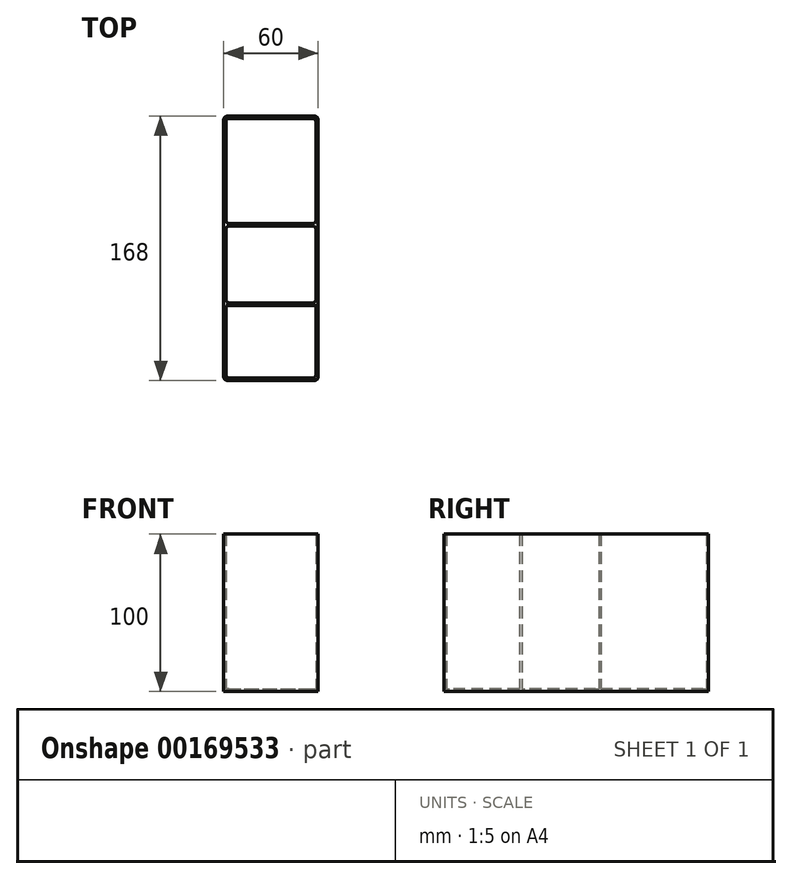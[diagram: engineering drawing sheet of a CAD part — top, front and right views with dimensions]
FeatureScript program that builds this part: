
annotation { "Feature Type Name" : "Feature", "Feature Type Description" : "" }
export const myFeature = defineFeature(function(context is Context, id is Id, definition is map)
    precondition{}
    {
        {
            var Q0;
            Q0=qCreatedBy(makeId("Top.planeOp"),FACE);
            var sketch = newSketch(context, id + "F0", { "sketchPlane" : qUnion([Q0])});
            skLineSegment(sketch, "E0.bottom", {"start": v(-30, 84) * mm, "end": v(30, 84) * mm});
            skLineSegment(sketch, "E0.top", {"start": v(-30, -84) * mm, "end": v(30, -84) * mm});
            skLineSegment(sketch, "E0.left", {"start": v(-30, 84) * mm, "end": v(-30, -84) * mm});
            skLineSegment(sketch, "E0.right", {"start": v(30, 84) * mm, "end": v(30, -84) * mm});
            skPoint(sketch, "E0.middle", {"position": v(0, 0) * mm});
            skSolve(sketch);
        }
        {
            var Q0;
            Q0 = qSketchRegion(id + "F0", true);
            extrude(context, id + "F1", {"entities" : qUnion([Q0]), "depth" : 100 * mm});
        }
        {
            var Q0;
            Q0=makeQuery(id+"F1.opExtrude","CAP_FACE",FACE,{"disambiguationData":[OSD([sQuery(id+"F0.wireOp",EDGE,"E0.bottom"),sQuery(id+"F0.wireOp",EDGE,"E0.top"),sQuery(id+"F0.wireOp",EDGE,"E0.left"),sQuery(id+"F0.wireOp",EDGE,"E0.right")])],"isStart":false});
            shell(context, id + "F2", {"entities" : qUnion([Q0]), "thickness" : 1.5 * mm});
        }
        {
            var Q0;
            Q0=makeQuery(id+"F2.opShell","OFFSET_FACE",FACE,{"disambiguationData":[OSD([sQuery(id+"F0.wireOp",EDGE,"E0.bottom"),sQuery(id+"F0.wireOp",EDGE,"E0.top"),sQuery(id+"F0.wireOp",EDGE,"E0.left"),sQuery(id+"F0.wireOp",EDGE,"E0.right")])]});
            var sketch = newSketch(context, id + "F3", { "sketchPlane" : qUnion([Q0])});
            skLineSegment(sketch, "E1", {"start": v(-28.5, 14.2) * mm, "end": v(28.5, 14.2) * mm});
            skLineSegment(sketch, "E2", {"start": v(-28.5, 15.7) * mm, "end": v(28.5, 15.7) * mm});
            skLineSegment(sketch, "E3", {"start": v(-28.5, -36.2) * mm, "end": v(28.5, -36.2) * mm});
            skLineSegment(sketch, "E4", {"start": v(-28.5, -34.7) * mm, "end": v(28.5, -34.7) * mm});
            skSolve(sketch);
        }
        {
            var Q0;
            {var subQ0=sQuery(id+"F3.wireOp",EDGE,"E1");Q0=makeQuery(id+"F3.imprint","IMPRINT",FACE,{"disambiguationData":[TD([[makeQuery(id+"F3.imprint","IMPRINT",EDGE,{"derivedFrom":subQ0}),1.0]])]});}
            var Q1;
            {var subQ0=sQuery(id+"F3.wireOp",EDGE,"E3");Q1=makeQuery(id+"F3.imprint","IMPRINT",FACE,{"disambiguationData":[TD([[makeQuery(id+"F3.imprint","IMPRINT",EDGE,{"derivedFrom":subQ0}),1.0]])]});}
            var Q2;
            Q2=makeQuery(id+"F1.opExtrude","CAP_FACE",FACE,{"disambiguationData":[OSD([sQuery(id+"F0.wireOp",EDGE,"E0.bottom"),sQuery(id+"F0.wireOp",EDGE,"E0.top"),sQuery(id+"F0.wireOp",EDGE,"E0.left"),sQuery(id+"F0.wireOp",EDGE,"E0.right")])],"isStart":false});
            extrude(context, id + "F4", {"entities" : qUnion([Q0, Q1]), "operationType" : NewBodyOperationType.ADD, "endBound" : BoundingType.UP_TO_SURFACE, "endBoundEntityFace" : qUnion([Q2]), "depth" : 25 * mm});
        }
        {
            var Q0;
            Q0=makeQuery(id+"F2.opShell","OFFSET_EDGE",EDGE,{"disambiguationData":[OSD([sQuery(id+"F0.wireOp",EDGE,"E0.top"),sQuery(id+"F0.wireOp",EDGE,"E0.left")])]});
            var Q1;
            Q1=makeQuery(id+"F4.opExtrude","SWEPT_EDGE",EDGE,{"disambiguationData":[OSD([sQuery(id+"F0.wireOp",EDGE,"E0.left"),sQuery(id+"F3.wireOp",EDGE,"E1")])]});
            var Q2;
            Q2=makeQuery(id+"F2.opShell","OFFSET_EDGE",EDGE,{"disambiguationData":[OSD([sQuery(id+"F0.wireOp",EDGE,"E0.bottom"),sQuery(id+"F0.wireOp",EDGE,"E0.left")])]});
            var Q3;
            Q3=makeQuery(id+"F2.opShell","OFFSET_EDGE",EDGE,{"disambiguationData":[OSD([sQuery(id+"F0.wireOp",EDGE,"E0.bottom"),sQuery(id+"F0.wireOp",EDGE,"E0.right")])]});
            var Q4;
            Q4=makeQuery(id+"F4.opExtrude","SWEPT_EDGE",EDGE,{"disambiguationData":[OSD([sQuery(id+"F0.wireOp",EDGE,"E0.right"),sQuery(id+"F3.wireOp",EDGE,"E2")])]});
            var Q5;
            Q5=makeQuery(id+"F2.opShell","OFFSET_EDGE",EDGE,{"disambiguationData":[OSD([sQuery(id+"F0.wireOp",EDGE,"E0.top"),sQuery(id+"F0.wireOp",EDGE,"E0.right")])]});
            var Q6;
            Q6=makeQuery(id+"F4.opExtrude","SWEPT_EDGE",EDGE,{"disambiguationData":[OSD([sQuery(id+"F0.wireOp",EDGE,"E0.right"),sQuery(id+"F3.wireOp",EDGE,"E1")])]});
            var Q7;
            Q7=makeQuery(id+"F4.opExtrude","SWEPT_EDGE",EDGE,{"disambiguationData":[OSD([sQuery(id+"F0.wireOp",EDGE,"E0.left"),sQuery(id+"F3.wireOp",EDGE,"E2")])]});
            var Q8;
            Q8=makeQuery(id+"F4.opExtrude","SWEPT_EDGE",EDGE,{"disambiguationData":[OSD([sQuery(id+"F0.wireOp",EDGE,"E0.left"),sQuery(id+"F3.wireOp",EDGE,"E3")])]});
            var Q9;
            Q9=makeQuery(id+"F4.opExtrude","SWEPT_EDGE",EDGE,{"disambiguationData":[OSD([sQuery(id+"F0.wireOp",EDGE,"E0.left"),sQuery(id+"F3.wireOp",EDGE,"E4")])]});
            var Q10;
            Q10=makeQuery(id+"F4.opExtrude","SWEPT_EDGE",EDGE,{"disambiguationData":[OSD([sQuery(id+"F0.wireOp",EDGE,"E0.right"),sQuery(id+"F3.wireOp",EDGE,"E4")])]});
            var Q11;
            Q11=makeQuery(id+"F4.opExtrude","SWEPT_EDGE",EDGE,{"disambiguationData":[OSD([sQuery(id+"F0.wireOp",EDGE,"E0.right"),sQuery(id+"F3.wireOp",EDGE,"E3")])]});
            fillet(context, id + "F5", {"entities" : qUnion([Q0, Q1, Q2, Q3, Q4, Q5, Q6, Q7, Q8, Q9, Q10, Q11]), "radius" : 2 * mm, "tangentPropagation" : true, "allowEdgeOverflow" : false});
        }
        {
            var Q0;
            Q0=makeQuery(id+"F1.opExtrude","SWEPT_EDGE",EDGE,{"disambiguationData":[OSD([sQuery(id+"F0.wireOp",EDGE,"E0.top"),sQuery(id+"F0.wireOp",EDGE,"E0.right")])]});
            var Q1;
            Q1=makeQuery(id+"F1.opExtrude","SWEPT_EDGE",EDGE,{"disambiguationData":[OSD([sQuery(id+"F0.wireOp",EDGE,"E0.top"),sQuery(id+"F0.wireOp",EDGE,"E0.left")])]});
            var Q2;
            Q2=makeQuery(id+"F1.opExtrude","SWEPT_EDGE",EDGE,{"disambiguationData":[OSD([sQuery(id+"F0.wireOp",EDGE,"E0.bottom"),sQuery(id+"F0.wireOp",EDGE,"E0.right")])]});
            var Q3;
            Q3=makeQuery(id+"F1.opExtrude","SWEPT_EDGE",EDGE,{"disambiguationData":[OSD([sQuery(id+"F0.wireOp",EDGE,"E0.bottom"),sQuery(id+"F0.wireOp",EDGE,"E0.left")])]});
            fillet(context, id + "F6", {"entities" : qUnion([Q0, Q1, Q2, Q3]), "radius" : 2.5 * mm, "tangentPropagation" : true, "allowEdgeOverflow" : false});
        }
    });
